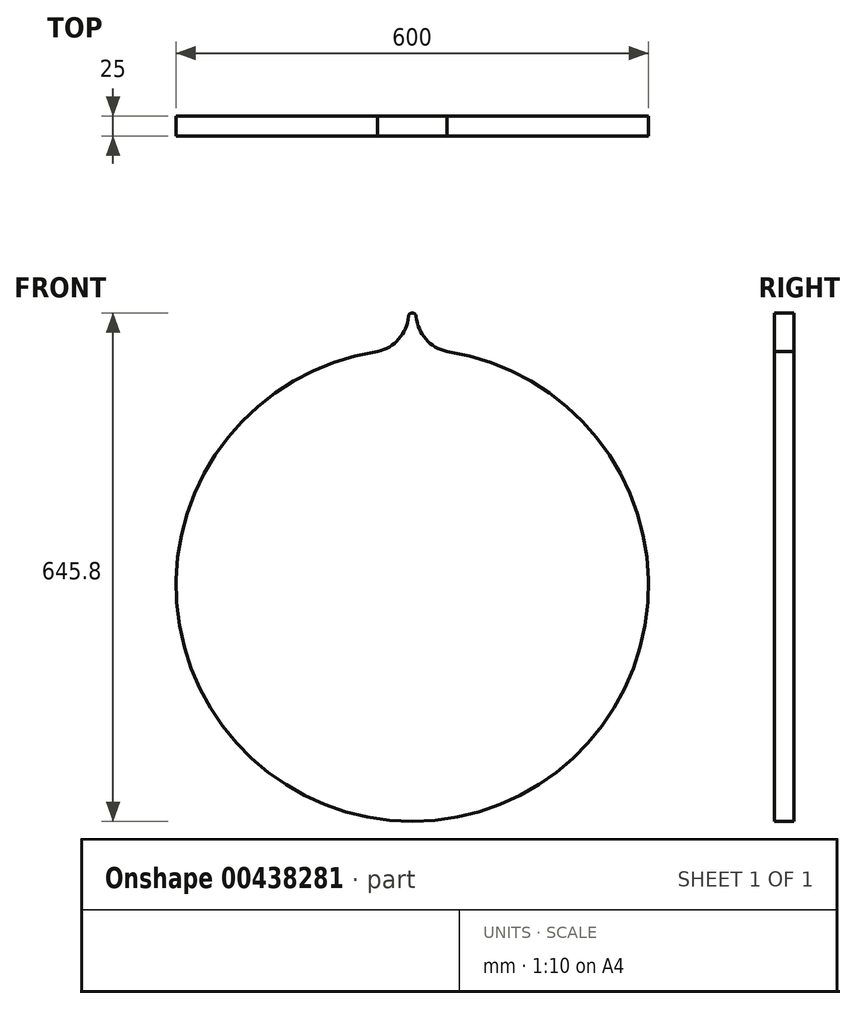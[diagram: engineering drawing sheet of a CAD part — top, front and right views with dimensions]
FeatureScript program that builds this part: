
annotation { "Feature Type Name" : "Feature", "Feature Type Description" : "" }
export const myFeature = defineFeature(function(context is Context, id is Id, definition is map)
    precondition{}
    {
        {
            var Q0;
            Q0=qCreatedBy(makeId("Front.planeOp"),FACE);
            var sketch = newSketch(context, id + "F0", { "sketchPlane" : qUnion([Q0])});
            skCircle(sketch, "E0", {"center": v(0, 0) * mm, "radius": 300 * mm});
            skSolve(sketch);
        }
        {
            var Q0;
            Q0 = qSketchRegion(id + "F0", true);
            extrude(context, id + "F1", {"entities" : qUnion([Q0]), "depth" : 25 * mm});
        }
        {
            var Q0;
            Q0=makeQuery(id+"F1.opExtrude","CAP_FACE",FACE,{"disambiguationData":[OSD([sQuery(id+"F0.wireOp",EDGE,"E0")])],"isStart":false});
            var sketch = newSketch(context, id + "F2", { "sketchPlane" : qUnion([Q0])});
            skArc(sketch, "E1", {"start": v(50, 295.8) * mm, "mid": v(0, 300) * mm, "end": v(-50, 295.8) * mm});
            skLineSegment(sketch, "E2", {"start": v(0, 0) * mm, "end": v(0, 332.68) * mm, "construction": true});
            skPoint(sketch, "E3", {"position": v(0, 300) * mm});
            skLineSegment(sketch, "E4", {"start": v(-50, 295.8) * mm, "end": v(50, 295.8) * mm, "construction": true});
            skArc(sketch, "E5", {"start": v(-50, 295.8) * mm, "mid": v(-19.28, 310.38) * mm, "end": v(-4.98, 341.24) * mm});
            skArc(sketch, "E6", {"start": v(4.98, 341.24) * mm, "mid": v(0, 345.8) * mm, "end": v(-4.98, 341.24) * mm});
            skPoint(sketch, "E7", {"position": v(0, 374.3) * mm});
            skPoint(sketch, "E7.positionSnap0", {"position": v(0, 345.8) * mm});
            skArc(sketch, "E8", {"start": v(4.98, 341.24) * mm, "mid": v(19.28, 310.38) * mm, "end": v(50, 295.8) * mm});
            skSolve(sketch);
        }
        {
            var Q0;
            Q0 = qSketchRegion(id + "F2", true);
            var Q1;
            Q1=makeQuery(id+"F1.opExtrude","CAP_FACE",FACE,{"disambiguationData":[OSD([sQuery(id+"F0.wireOp",EDGE,"E0")])],"isStart":true});
            extrude(context, id + "F3", {"entities" : qUnion([Q0]), "operationType" : NewBodyOperationType.ADD, "endBound" : BoundingType.UP_TO_SURFACE, "oppositeDirection" : true, "endBoundEntityFace" : qUnion([Q1]), "depth" : 25 * mm});
        }
        {
            var Q0;
            Q0=qCreatedBy(makeId("Right.planeOp"),FACE);
            var sketch = newSketch(context, id + "F4", { "sketchPlane" : qUnion([Q0])});
            skLineSegment(sketch, "E9", {"start": v(0, 0) * mm, "end": v(121.28, 0) * mm});
            skSolve(sketch);
        }
    });
